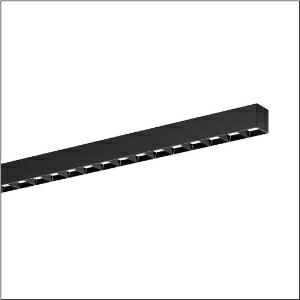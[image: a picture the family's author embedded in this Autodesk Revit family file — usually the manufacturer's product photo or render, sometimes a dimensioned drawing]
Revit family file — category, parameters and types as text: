
# Revit family: silica_r__21_51mx21dc3abb_8748
name_source: partatom
category: Lighting Fixtures
units: mm (PartAtom-declared; Revit-internal decimal feet)

## family parameters
Cut with Voids When Loaded = No
Host = Face
Light Source = No
Part Type = Normal
Room Calculation Point = No
Round Connector Dimension = Use Diameter
Shared = No

## types (1)
- --- (1 x LED, 10800 lm, 69.3 W, 3000K)
    Apparent Load = 69 VA
    CIE Flux Codes = 87 99 100 100 100
    Color Rendering = 80
    Color Temperature = 3000K
    Default Elevation = 1800 mm
    Description = Silica® 21, office luminaire, primary light control with darklight reflector, of PMMA, black, CAT 2 (L<= 3000cd/m²), light emission: direct distribution, primary light characteristic: symmetric, installation type: surface-mounted, LED, rated luminous flux: 10.800lm, luminous efficacy: 156lm/W, light colour: 830, colour temperature: 3000K, with terminal, 3+2-pole, max. 2.5mm², mains connection: 220..240V, AC, 50/60Hz, luminaire housing, of aluminium, jet black (RAL 9005), length: 3.004mm, width: 53mm, height: 53mm, protection rating (complete): IP20, insulation class (complete): insulation class I (protective earthing), certification: CE, permissible operating ambient temperature: 0..+35°C, standard: EN 50419, packaging unit: 1 piece
    Height = 0 mm  [stored 0 ft]
    Lamp = 1 x LED
    Lamp Light Flux = 10800 lm
    Lamp Power = 69.3 W
    Lamp count = 1
    Length = 3004 mm
    Luminous efficacy = 156 lm/W
    Manufacturer = Siteco
    ModVariant = No
    Model = 51MX21DC3ABB
    Mounting Place = Ceiling
    Mounting Type = Recessed
    Number of Poles = 1
    OnlyDefault = Yes
    Power Factor = 1
    Product Name = Silica® 21
    Product group = office luminaire | ceiling recessed
    ProductGroupID = 400
    Protection Class = Protection class I
    Protection Degree = IP 20
    RLX_Detail_Level = 1
    RLX_Emergency_Light_Flux = 0 lm
    RLX_Emergency_Type = 0
    RLX_Emergency_Type_DB = No
    RlxData = <blob elided: 64925 chars, md5=b5cc244c>
    Socket = socket
    Standby Power = 0 W
    System Light Flux = 10800 lm
    System Power = 69 W
    Type Comments = factory setting: luminous flux: 100 % | dim-lin: 254 | 393 mA
    Type Image = l_1335908.jpg
    URL = http://relux.com
    VarID = @adj_093335
    Voltage = 0 V
    Weight = 0.00 kg
    Width = 53 mm

note: [stored X ft] marks values corroborated as IEEE doubles in the binary element streams (Revit-internal decimal feet)

## geometry (parser evidence)
native form markers: Blend x4, Sweep x10
no freeform markers — native parametric forms only
